# Revit family: Maxlogic alarm matrix panel
name_source: partatom
category: Fire Alarm Devices
units: mm (PartAtom-declared; Revit-internal decimal feet)

## family parameters
Cut with Voids When Loaded = No
Host = Face
Maintain Annotation Orientation = Yes
OmniClass Number = 23.85.30.21
OmniClass Title = Environmental Detection/Registration
Part Type = Normal
Room Calculation Point = No
Round Connector Dimension = Use Diameter
Shared = No

## types (1)
- Maxlogic Anons/Alarm Matrix Paneli, 19", 3U Rack yapısında, anons güç modülü anons çıkış modülü dahil
    Announce / alarm matrix blank panel = MLY-5001
    Announce input module = ML-5020.AI 4 adres alır
    Battery = 2 X ( 12V 7Ah )
    Code Performance = EN 54-16
    Color = Siyah
    Cost = 0 $
    Default Elevation = 0 mm  [stored 0 ft]
    Description = Anons/Alarm Matrix Paneli, 19", 3U Rack yapısında, anons güç modülü anons çıkış modülü dahil
    Device Adress Setup = El tipi adresleme cihazı
    External supply = 220 V/AC
    Fax Number = (+)90 216 466 45 10
    Installation Manual = https://mavilielektronik.com
    Main Material = Metal Red
    Manufacturer = Mavili Elektronik Ticaret A.Ş.
    Model = Maxlogic
    Mounting surface = Rack kabine montaj
    Nominal Depth = 209 mm
    Nominal Height = 133 mm
    Nominal Wıdth = 483 mm
    Operating temperature = (-10°C) - (+55°C)
    Operating voltage range = 28 V /DC
    Operatonal Voltage (default) = 28 V /DC
    Product Code = ML-5020
    Programmable alarm / alert output module = ML-5020.PO 8 adres alır
    Secondary Material = Plexiglas
    URL = https://www.mavili.com.tr
    Warranty Duration Labor = 2
    Warranty Duration Parts = 2
    Warranty Duration Unit = Year

note: [stored X ft] marks values corroborated as IEEE doubles in the binary element streams (Revit-internal decimal feet)

## geometry (parser evidence)
native form markers: Sweep x2
no freeform markers — native parametric forms only
